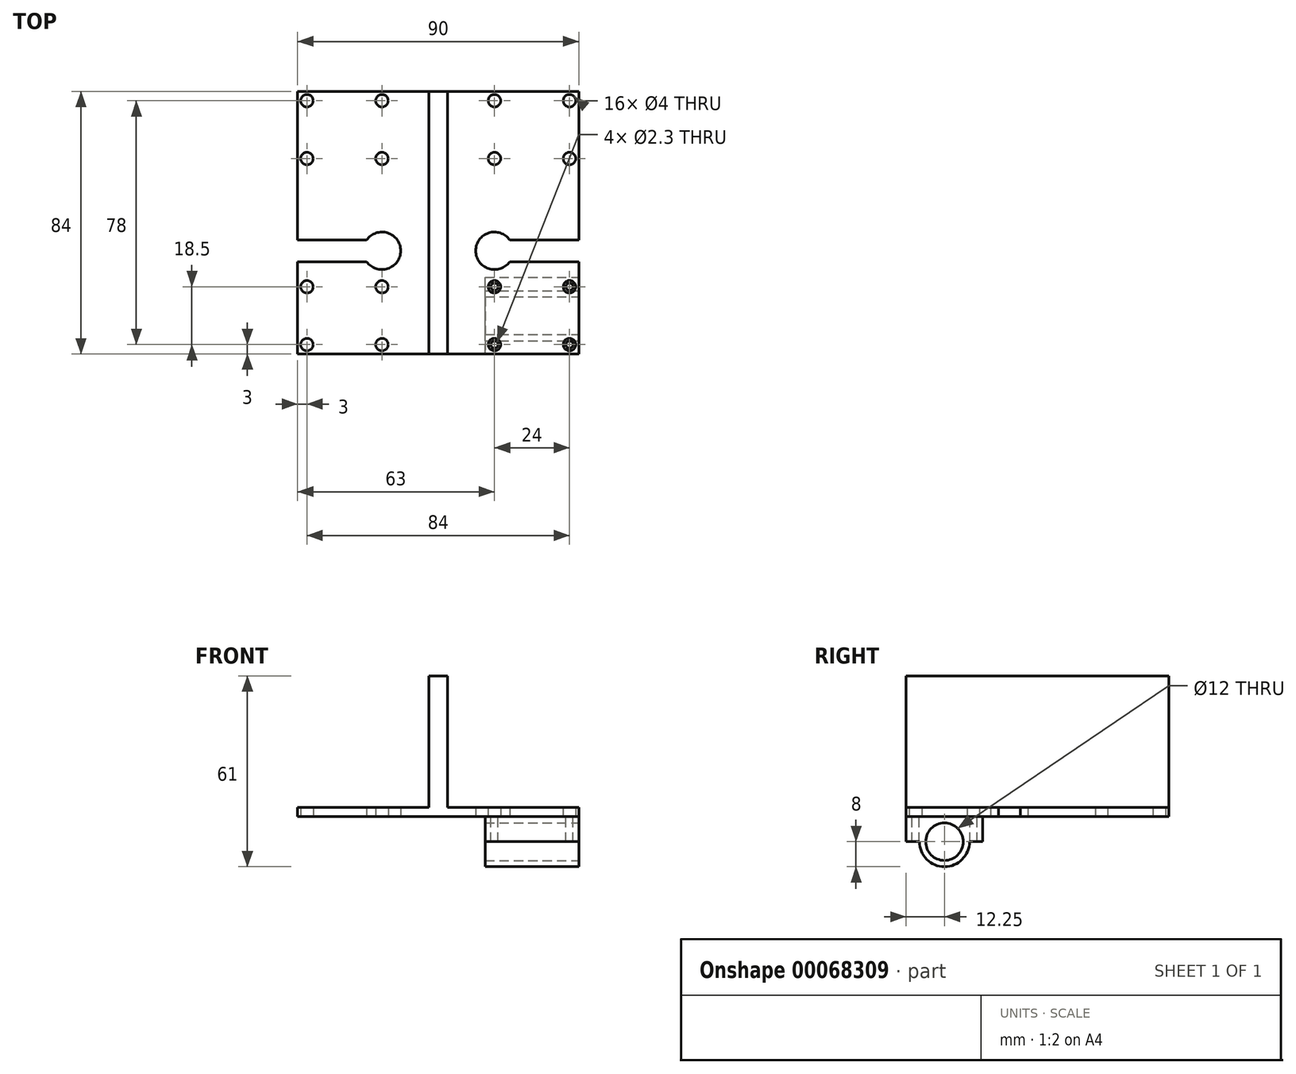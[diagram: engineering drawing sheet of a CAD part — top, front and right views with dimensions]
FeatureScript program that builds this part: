
annotation { "Feature Type Name" : "Feature", "Feature Type Description" : "" }
export const myFeature = defineFeature(function(context is Context, id is Id, definition is map)
    precondition{}
    {
        {
            var Q0;
            Q0=qCreatedBy(makeId("Front.planeOp"),FACE);
            var sketch = newSketch(context, id + "F0", { "sketchPlane" : qUnion([Q0])});
            skLineSegment(sketch, "E0", {"start": v(0, 45) * mm, "end": v(0, 0) * mm});
            skLineSegment(sketch, "E1", {"start": v(0, 0) * mm, "end": v(45, 0) * mm});
            skLineSegment(sketch, "E2", {"start": v(45, 0) * mm, "end": v(45, 3) * mm});
            skLineSegment(sketch, "E3", {"start": v(45, 3) * mm, "end": v(3, 3) * mm});
            skLineSegment(sketch, "E4", {"start": v(3, 3) * mm, "end": v(3, 45) * mm});
            skLineSegment(sketch, "E5", {"start": v(3, 45) * mm, "end": v(0, 45) * mm});
            skLineSegment(sketch, "E6.MirrorCS", {"start": v(-3, 45) * mm, "end": v(0, 45) * mm});
            skLineSegment(sketch, "E7.MirrorCS", {"start": v(-45, 0) * mm, "end": v(-45, 3) * mm});
            skLineSegment(sketch, "E8.MirrorCS", {"start": v(-3, 3) * mm, "end": v(-3, 45) * mm});
            skLineSegment(sketch, "E9.MirrorCS", {"start": v(-45, 3) * mm, "end": v(-3, 3) * mm});
            skLineSegment(sketch, "E10.MirrorCS", {"start": v(0, 0) * mm, "end": v(-45, 0) * mm});
            skSolve(sketch);
        }
        {
            var Q0;
            Q0 = qSketchRegion(id + "F0", true);
            extrude(context, id + "F1", {"entities" : qUnion([Q0]), "endBound" : BoundingType.SYMMETRIC, "depth" : 84 * mm});
        }
        {
            var Q0;
            Q0=makeQuery(id+"F1.opExtrude","SWEPT_FACE",FACE,{"disambiguationData":[OSD([sQuery(id+"F0.wireOp",EDGE,"E1"),sQuery(id+"F0.wireOp",EDGE,"E10.MirrorCS")])]});
            var sketch = newSketch(context, id + "F2", { "sketchPlane" : qUnion([Q0])});
            skArc(sketch, "E11", {"start": v(22.87, 12.5) * mm, "mid": v(12, 9) * mm, "end": v(22.87, 5.5) * mm});
            skCircle(sketch, "E12", {"center": v(35, 9) * mm, "radius": 1.5 * mm, "construction": true});
            skLineSegment(sketch, "E13", {"start": v(22.87, 12.5) * mm, "end": v(45, 12.5) * mm});
            skLineSegment(sketch, "E14", {"start": v(22.87, 5.5) * mm, "end": v(45, 5.5) * mm});
            skLineSegment(sketch, "E15", {"start": v(22.87, 12.5) * mm, "end": v(22.87, 5.5) * mm, "construction": true});
            skLineSegment(sketch, "E16", {"start": v(22.87, 9) * mm, "end": v(18, 9) * mm, "construction": true});
            skLineSegment(sketch, "E17", {"start": v(45, 12.5) * mm, "end": v(45, 5.5) * mm});
            skArc(sketch, "E18.MirrorCS", {"start": v(-22.87, 12.5) * mm, "mid": v(-12, 9) * mm, "end": v(-22.87, 5.5) * mm});
            skLineSegment(sketch, "E19.MirrorCS", {"start": v(-45, 12.5) * mm, "end": v(-45, 5.5) * mm});
            skLineSegment(sketch, "E20.MirrorCS", {"start": v(-22.87, 12.5) * mm, "end": v(-22.87, 5.5) * mm, "construction": true});
            skLineSegment(sketch, "E21.MirrorCS", {"start": v(-22.87, 9) * mm, "end": v(-18, 9) * mm, "construction": true});
            skLineSegment(sketch, "E22.MirrorCS", {"start": v(-22.87, 5.5) * mm, "end": v(-45, 5.5) * mm});
            skLineSegment(sketch, "E23.MirrorCS", {"start": v(-22.87, 12.5) * mm, "end": v(-45, 12.5) * mm});
            skCircle(sketch, "E24.MirrorC", {"center": v(-35, 9) * mm, "radius": 1.5 * mm, "construction": true});
            skSolve(sketch);
        }
        {
            var Q0;
            Q0 = qSketchRegion(id + "F2", true);
            extrude(context, id + "F3", {"entities" : qUnion([Q0]), "operationType" : NewBodyOperationType.REMOVE, "endBound" : BoundingType.THROUGH_ALL, "oppositeDirection" : true, "depth" : 25 * mm});
        }
        {
            var Q0;
            {var subQ2=sQuery(id+"F0.wireOp",EDGE,"E2");Q0=makeQuery(id+"F3.boolean.opBoolean","SPLIT",FACE,{"disambiguationData":[TD([makeQuery(id+"F3.opExtrude","SWEPT_FACE",FACE,{"disambiguationData":[OSD([sQuery(id+"F2.wireOp",EDGE,"E13")])]})])],"derivedFrom":makeQuery(id+"F1.opExtrude","SWEPT_FACE",FACE,{"disambiguationData":[OSD([subQ2])]})});}
            var sketch = newSketch(context, id + "F4", { "sketchPlane" : qUnion([Q0])});
            skLineSegment(sketch, "E25", {"start": v(-42, 0) * mm, "end": v(-42, -8) * mm});
            skLineSegment(sketch, "E26", {"start": v(-17.5, 0) * mm, "end": v(-17.5, -16) * mm});
            skLineSegment(sketch, "E27", {"start": v(-42, 0) * mm, "end": v(-17.5, 0) * mm});
            skCircle(sketch, "E28", {"center": v(-29.75, -8) * mm, "radius": 6 * mm});
            skLineSegment(sketch, "E29", {"start": v(-29.75, 0) * mm, "end": v(-29.75, -8) * mm, "construction": true});
            skArc(sketch, "E30", {"start": v(-21.75, -8) * mm, "mid": v(-29.75, -16) * mm, "end": v(-37.75, -8) * mm});
            skLineSegment(sketch, "E31", {"start": v(-21.75, -8) * mm, "end": v(-17.5, -8) * mm});
            skLineSegment(sketch, "E32", {"start": v(-37.75, -8) * mm, "end": v(-42, -8) * mm});
            skPoint(sketch, "E33.orphan", {"position": v(-42, -16) * mm});
            skSolve(sketch);
        }
        {
            var Q0;
            Q0 = qSketchRegion(id + "F4", true);
            extrude(context, id + "F5", {"entities" : qUnion([Q0]), "oppositeDirection" : true, "depth" : 30 * mm});
        }
        {
            var Q0;
            Q0=makeQuery(id+"F5.opExtrude","SWEPT_FACE",FACE,{"disambiguationData":[OSD([sQuery(id+"F4.wireOp",EDGE,"E27")])]});
            var sketch = newSketch(context, id + "F6", { "sketchPlane" : qUnion([Q0])});
            skCircle(sketch, "E34", {"center": v(18, -20.5) * mm, "radius": 1.15 * mm});
            skLineSegment(sketch, "E35", {"start": v(18, -17.5) * mm, "end": v(18, -42) * mm, "construction": true});
            skLineSegment(sketch, "E36", {"start": v(15, -20.5) * mm, "end": v(45, -20.5) * mm, "construction": true});
            skLineSegment(sketch, "E37", {"start": v(15, -29.75) * mm, "end": v(45, -29.75) * mm, "construction": true});
            skLineSegment(sketch, "E38", {"start": v(30, -17.5) * mm, "end": v(30, -42) * mm, "construction": true});
            skLineSegment(sketch, "E39.MirrorCS", {"start": v(15, -39) * mm, "end": v(45, -39) * mm, "construction": true});
            skLineSegment(sketch, "E40.MirrorCS", {"start": v(18, -42) * mm, "end": v(18, -17.5) * mm, "construction": true});
            skCircle(sketch, "E41.MirrorC", {"center": v(18, -39) * mm, "radius": 1.15 * mm});
            skCircle(sketch, "E42.MirrorC", {"center": v(42, -20.5) * mm, "radius": 1.15 * mm});
            skCircle(sketch, "E43.MirrorC", {"center": v(42, -39) * mm, "radius": 1.15 * mm});
            skSolve(sketch);
        }
        {
            var Q0;
            Q0 = qSketchRegion(id + "F6", true);
            extrude(context, id + "F7", {"entities" : qUnion([Q0]), "operationType" : NewBodyOperationType.REMOVE, "endBound" : BoundingType.THROUGH_ALL, "oppositeDirection" : true, "depth" : 10 * mm});
        }
        {
            var Q0;
            Q0=makeQuery(id+"F1.opExtrude","SWEPT_FACE",FACE,{"disambiguationData":[OSD([sQuery(id+"F0.wireOp",EDGE,"E1"),sQuery(id+"F0.wireOp",EDGE,"E10.MirrorCS")])]});
            var sketch = newSketch(context, id + "F8", { "sketchPlane" : qUnion([Q0])});
            skCircle(sketch, "E44", {"center": v(18, 20.5) * mm, "radius": 2 * mm});
            skCircle(sketch, "E45", {"center": v(18, 39) * mm, "radius": 2 * mm});
            skCircle(sketch, "E46", {"center": v(42, 20.5) * mm, "radius": 2 * mm});
            skCircle(sketch, "E47", {"center": v(42, 39) * mm, "radius": 2 * mm});
            skCircle(sketch, "E48.MirrorC", {"center": v(18, -20.5) * mm, "radius": 2 * mm});
            skCircle(sketch, "E49.MirrorC", {"center": v(18, -39) * mm, "radius": 2 * mm});
            skCircle(sketch, "E50.MirrorC", {"center": v(42, -20.5) * mm, "radius": 2 * mm});
            skCircle(sketch, "E51.MirrorC", {"center": v(42, -39) * mm, "radius": 2 * mm});
            skCircle(sketch, "E52.MirrorC", {"center": v(-42, -39) * mm, "radius": 2 * mm});
            skCircle(sketch, "E53.MirrorC", {"center": v(-42, -20.5) * mm, "radius": 2 * mm});
            skCircle(sketch, "E54.MirrorC", {"center": v(-18, -39) * mm, "radius": 2 * mm});
            skCircle(sketch, "E55.MirrorC", {"center": v(-18, -20.5) * mm, "radius": 2 * mm});
            skCircle(sketch, "E56.MirrorC", {"center": v(-42, 39) * mm, "radius": 2 * mm});
            skCircle(sketch, "E57.MirrorC", {"center": v(-42, 20.5) * mm, "radius": 2 * mm});
            skCircle(sketch, "E58.MirrorC", {"center": v(-18, 39) * mm, "radius": 2 * mm});
            skCircle(sketch, "E59.MirrorC", {"center": v(-18, 20.5) * mm, "radius": 2 * mm});
            skSolve(sketch);
        }
        {
            var Q0;
            Q0 = qSketchRegion(id + "F8", true);
            extrude(context, id + "F9", {"entities" : qUnion([Q0]), "operationType" : NewBodyOperationType.REMOVE, "endBound" : BoundingType.THROUGH_ALL, "oppositeDirection" : true, "depth" : 25 * mm});
        }
    });
